# Revit family: Enclosed_Safety_Shower-Bradley_Corp-S19372
name_source: partatom
category: Plumbing Fixtures
revit_build: Autodesk Revit 2018 (Build: 20170223_1515(x64)
units: mm (PartAtom-declared; Revit-internal decimal feet)

## family parameters
Always vertical = Yes
Cut with Voids When Loaded = No
Part Type = Normal
Room Calculation Point = No
Round Connector Dimension = Use Radius
Shared = No
Work Plane-Based = No

## types (1)
- S19372
    ADA Compliant = No
    Apparent Load = 0 VA
    Assembly Code = D2010700
    B.O. Roof Panel = 82.25 "
    Buy American Act = To Be Determined
    Cold Water Connection Diameter = 1"
    Cold Water Connection Radius = 1"
    Depth = 0 "
    Description = Enclosed Indoor Shower with Electric Tankless Water Heater
    Drain Location - Center = No
    Drain Location - Left = No
    Drain Location - Right = Yes
    Floor to T.O. Roof Panel = 99.75 "
    Frequency = 0 Hz
    Height = 109 "
    Installation Type = Floor Mounted
    Length = 57.25 "
    Low Emitting Finish = Yes
    Low Emitting Material = Yes
    Manufacturer = Bradley Corporation
    MasterFormat Number = 22 45 13
    MasterFormat Title = Emergency Showers
    Model = S19372
    Number of Poles = 1
    OmniClass Code = 23-29 37 15
    OmniClass Title = Emergency Showers
    Percentage of Recycled Content = 0
    Power Factor = 0
    T.O. Wall Panel = 80.94 "
    Type Comments = S19372
    URL = http://www.bradleycorp.com
    Version = 1.0
    Voltage = 120 V
    Waste Water Connection Diameter = 3"
    Waste Water Connection Radius = 2"
    Wattage = 0 W
    Width = 57.25 "

## geometry (parser evidence)
native form markers: Blend x8, Sweep x9
no freeform markers — native parametric forms only
